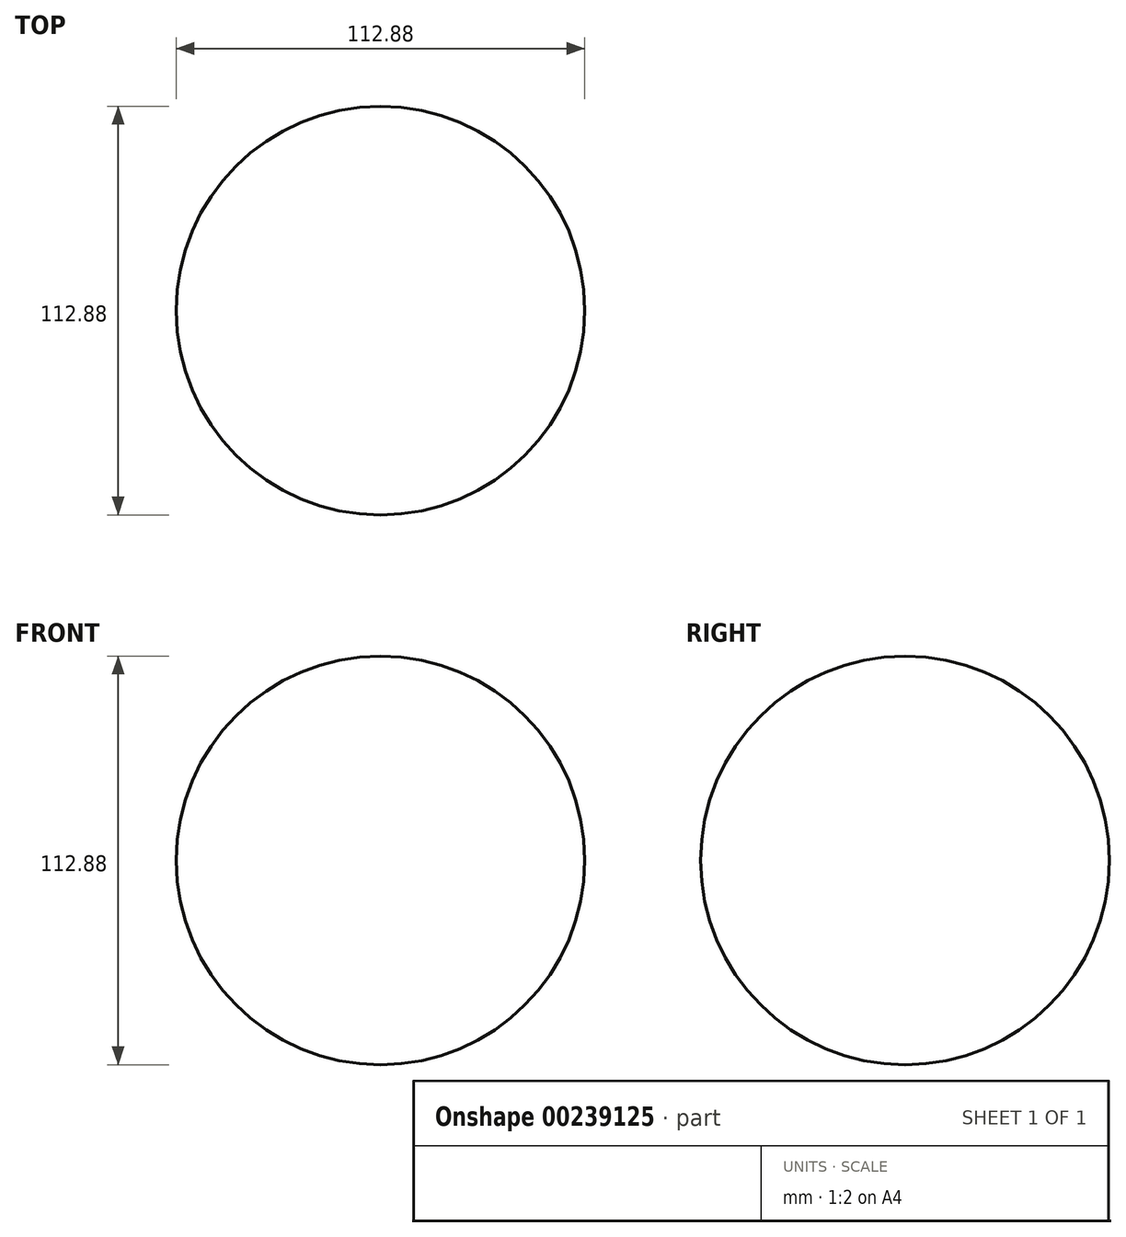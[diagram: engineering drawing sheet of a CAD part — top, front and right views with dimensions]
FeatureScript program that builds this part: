
annotation { "Feature Type Name" : "Feature", "Feature Type Description" : "" }
export const myFeature = defineFeature(function(context is Context, id is Id, definition is map)
    precondition{}
    {
        {
            var Q0;
            Q0=qCreatedBy(makeId("Front.planeOp"),FACE);
            var sketch = newSketch(context, id + "F0", { "sketchPlane" : qUnion([Q0])});
            skArc(sketch, "E0", {"start": v(0, -56.44) * mm, "mid": v(56.44, 0) * mm, "end": v(0, 56.44) * mm});
            skLineSegment(sketch, "E1", {"start": v(0, 56.44) * mm, "end": v(0, -56.44) * mm});
            skSolve(sketch);
        }
        {
            var Q0;
            Q0 = qSketchRegion(id + "F0", true);
            var Q1;
            Q1=sQuery(id+"F0.wireOp",EDGE,"E1");
            revolve(context, id + "F1", {"entities" : qUnion([Q0]), "axis" : qUnion([Q1]), "revolveType" : RevolveType.FULL});
        }
    });
